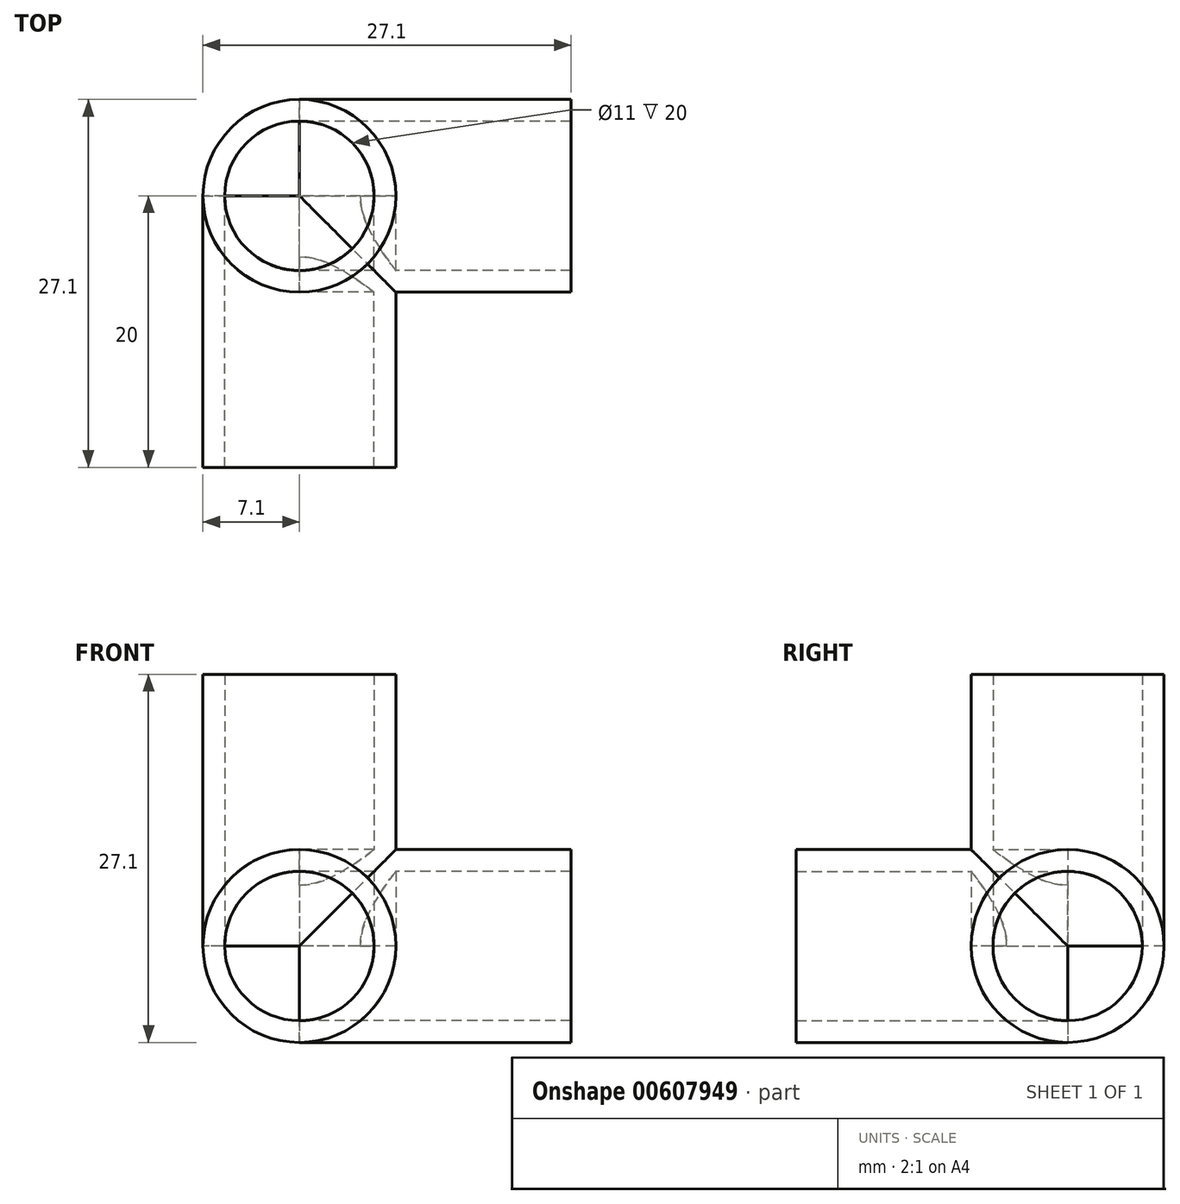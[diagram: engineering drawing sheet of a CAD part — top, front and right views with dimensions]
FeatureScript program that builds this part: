
annotation { "Feature Type Name" : "Feature", "Feature Type Description" : "" }
export const myFeature = defineFeature(function(context is Context, id is Id, definition is map)
    precondition{}
    {
        {
            var Q0;
            Q0=qCreatedBy(makeId("Top.planeOp"),FACE);
            var sketch = newSketch(context, id + "F0", { "sketchPlane" : qUnion([Q0])});
            skLineSegment(sketch, "E0", {"start": v(0, 0) * mm, "end": v(20, 0) * mm, "construction": true});
            skLineSegment(sketch, "E1", {"start": v(0, 0) * mm, "end": v(0, -20) * mm, "construction": true});
            skCircle(sketch, "E2", {"center": v(0, 0) * mm, "radius": 5.5 * mm});
            skCircle(sketch, "E3", {"center": v(0, 0) * mm, "radius": 7.1 * mm});
            skSolve(sketch);
        }
        {
            var Q0;
            Q0=qCreatedBy(makeId("Front.planeOp"),FACE);
            var sketch = newSketch(context, id + "F1", { "sketchPlane" : qUnion([Q0])});
            skLineSegment(sketch, "E4", {"start": v(0, 0) * mm, "end": v(0, 20) * mm, "construction": true});
            skCircle(sketch, "E5", {"center": v(0, 0) * mm, "radius": 5.5 * mm});
            skCircle(sketch, "E6", {"center": v(0, 0) * mm, "radius": 7.1 * mm});
            skSolve(sketch);
        }
        {
            var Q0;
            Q0=qCreatedBy(makeId("Right.planeOp"),FACE);
            var sketch = newSketch(context, id + "F2", { "sketchPlane" : qUnion([Q0])});
            skCircle(sketch, "E7", {"center": v(0, 0) * mm, "radius": 5.5 * mm});
            skCircle(sketch, "E8", {"center": v(0, 0) * mm, "radius": 7.1 * mm});
            skSolve(sketch);
        }
        {
            var Q0;
            Q0=makeQuery(id+"F2.imprint","IMPRINT",FACE,{"disambiguationData":[TD([[makeQuery(id+"F2.imprint","IMPRINT",EDGE,{"derivedFrom":sQuery(id+"F2.wireOp",EDGE,"E7")}),-1.0]])]});
            extrude(context, id + "F3", {"entities" : qUnion([Q0]), "depth" : 20 * mm, "offsetDistance" : 25 * mm});
        }
        {
            var Q0;
            Q0=makeQuery(id+"F1.imprint","IMPRINT",FACE,{"disambiguationData":[TD([[makeQuery(id+"F1.imprint","IMPRINT",EDGE,{"derivedFrom":sQuery(id+"F1.wireOp",EDGE,"E5")}),-1.0]])]});
            extrude(context, id + "F4", {"entities" : qUnion([Q0]), "operationType" : NewBodyOperationType.ADD, "depth" : 20 * mm, "offsetDistance" : 25 * mm});
        }
        {
            var Q0;
            Q0=makeQuery(id+"F0.imprint","IMPRINT",FACE,{"disambiguationData":[TD([[makeQuery(id+"F0.imprint","IMPRINT",EDGE,{"derivedFrom":sQuery(id+"F0.wireOp",EDGE,"E2")}),-1.0]])]});
            extrude(context, id + "F5", {"entities" : qUnion([Q0]), "operationType" : NewBodyOperationType.ADD, "depth" : 20 * mm, "offsetDistance" : 25 * mm});
        }
    });
